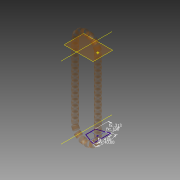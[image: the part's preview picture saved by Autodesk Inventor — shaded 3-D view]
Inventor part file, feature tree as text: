
AUTODESK INVENTOR PART (.ipt)
format: ipt  version: 2014 SP1 (Build 180222100, 222)  size: 223,232 bytes
history: native  units: mm (DEFAULTED — no unit token found)
features: other x45, extrude x40, sketch x2, plane x1, pattern_linear x1
ambient origin geometry x8: Origin, YZ Plane, XZ Plane, XY Plane, X Axis, Y Axis, Z Axis, Center Point
bodies: Body1 (feature_tree), Body2 (feature_tree), Body3 (feature_tree), Body4 (feature_tree), Body5 (feature_tree), Body6 (feature_tree), Body7 (feature_tree), Body8 (feature_tree), Body9 (feature_tree), Body10 (feature_tree), Body11 (feature_tree), Body12 (feature_tree), Body13 (feature_tree), Body14 (feature_tree), Body15 (feature_tree), Body16 (feature_tree), Body17 (feature_tree), Body18 (feature_tree), Body19 (feature_tree), Body20 (feature_tree), Body21 (feature_tree), Body22 (feature_tree), Body23 (feature_tree), Body24 (feature_tree), Body25 (feature_tree), Body26 (feature_tree), Body27 (feature_tree), Body28 (feature_tree), Body29 (feature_tree), Body30 (feature_tree), Body31 (feature_tree), Body32 (feature_tree), Body33 (feature_tree), Body34 (feature_tree), Body35 (feature_tree), Body36 (feature_tree), Body37 (feature_tree), Body38 (feature_tree), Body39 (feature_tree), Body40 (feature_tree)
feature tree (89):
  sketch  "Sketch Path"  dims[d1=10.6172mm d2=7.9375mm d3=2.682204mm d5=6.981317mm d7=0.0mm d8=0.0mm d9=0.0mm d10=2.54mm d11=0.0mm d12=400.0mm]
  other  "Cross Section Plane"
  other  "Work Axis1"
  other  "Work Axis2"
  other  "Cross Section"
  other  "Work Point1"
  plane  "Work Plane2"
  pattern_linear  "Rectangular Pattern1"  Spacing1=7.9375mm  [1 undecoded]
  sketch  "Sketch3"  dims[d0=0.0mm]
  other  "Srf1"
  other  "Srf2"
  other  "Srf3"
  other  "Srf4"
  other  "Srf5"
  other  "Srf6"
  other  "Srf7"
  other  "Srf8"
  other  "Srf9"
  other  "Srf10"
  other  "Srf11"
  other  "Srf12"
  other  "Srf13"
  other  "Srf14"
  other  "Srf15"
  other  "Srf16"
  other  "Srf17"
  other  "Srf18"
  other  "Srf19"
  other  "Srf20"
  other  "Srf21"
  other  "Srf22"
  other  "Srf23"
  other  "Srf24"
  other  "Srf25"
  other  "Srf26"
  other  "Srf27"
  other  "Srf28"
  other  "Srf29"
  other  "Srf30"
  other  "Srf31"
  other  "Srf32"
  other  "Srf33"
  other  "Srf34"
  other  "Srf35"
  other  "Srf36"
  other  "Srf37"
  other  "Srf38"
  other  "Srf41"
  other  "Srf42"
  extrude  "ExtrusionSrf1"  Depth=2.682204mm
  extrude  "ExtrusionSrf2"  Depth=6.981317mm
  extrude  "ExtrusionSrf3"  TaperAngle=0.0deg  [1 undecoded]
  extrude  "ExtrusionSrf4"  Depth=2.54mm TaperAngle=0.0deg
  extrude  "ExtrusionSrf5"  Depth=400.0mm
  extrude  "ExtrusionSrf6"  [1 undecoded]
  extrude  "ExtrusionSrf7"  [1 undecoded]
  extrude  "ExtrusionSrf8"  [1 undecoded]
  extrude  "ExtrusionSrf9"  [1 undecoded]
  extrude  "ExtrusionSrf10"  [1 undecoded]
  extrude  "ExtrusionSrf11"  [1 undecoded]
  extrude  "ExtrusionSrf12"  [1 undecoded]
  extrude  "ExtrusionSrf13"  [1 undecoded]
  extrude  "ExtrusionSrf14"  [1 undecoded]
  extrude  "ExtrusionSrf15"  [1 undecoded]
  extrude  "ExtrusionSrf16"  [1 undecoded]
  extrude  "ExtrusionSrf17"  [1 undecoded]
  extrude  "ExtrusionSrf18"  [1 undecoded]
  extrude  "ExtrusionSrf19"  [1 undecoded]
  extrude  "ExtrusionSrf20"  [1 undecoded]
  extrude  "ExtrusionSrf21"  [1 undecoded]
  extrude  "ExtrusionSrf22"  [1 undecoded]
  extrude  "ExtrusionSrf23"  [1 undecoded]
  extrude  "ExtrusionSrf24"  [1 undecoded]
  extrude  "ExtrusionSrf25"  [1 undecoded]
  extrude  "ExtrusionSrf26"  [1 undecoded]
  extrude  "ExtrusionSrf27"  [1 undecoded]
  extrude  "ExtrusionSrf28"  [1 undecoded]
  extrude  "ExtrusionSrf29"  [1 undecoded]
  extrude  "ExtrusionSrf30"  [1 undecoded]
  extrude  "ExtrusionSrf31"  [1 undecoded]
  extrude  "ExtrusionSrf32"  [1 undecoded]
  extrude  "ExtrusionSrf33"  [1 undecoded]
  extrude  "ExtrusionSrf34"  [1 undecoded]
  extrude  "ExtrusionSrf35"  [1 undecoded]
  extrude  "ExtrusionSrf36"  [1 undecoded]
  extrude  "ExtrusionSrf37"  [1 undecoded]
  extrude  "ExtrusionSrf38"  [1 undecoded]
  extrude  "ExtrusionSrf41"  [1 undecoded]
  extrude  "ExtrusionSrf42"  [1 undecoded]
note: 37 required parameter values undecoded (feature->parameter linkage not recoverable at this tier; creation-order binding heuristic only, values carry confidence <= 0.55)
